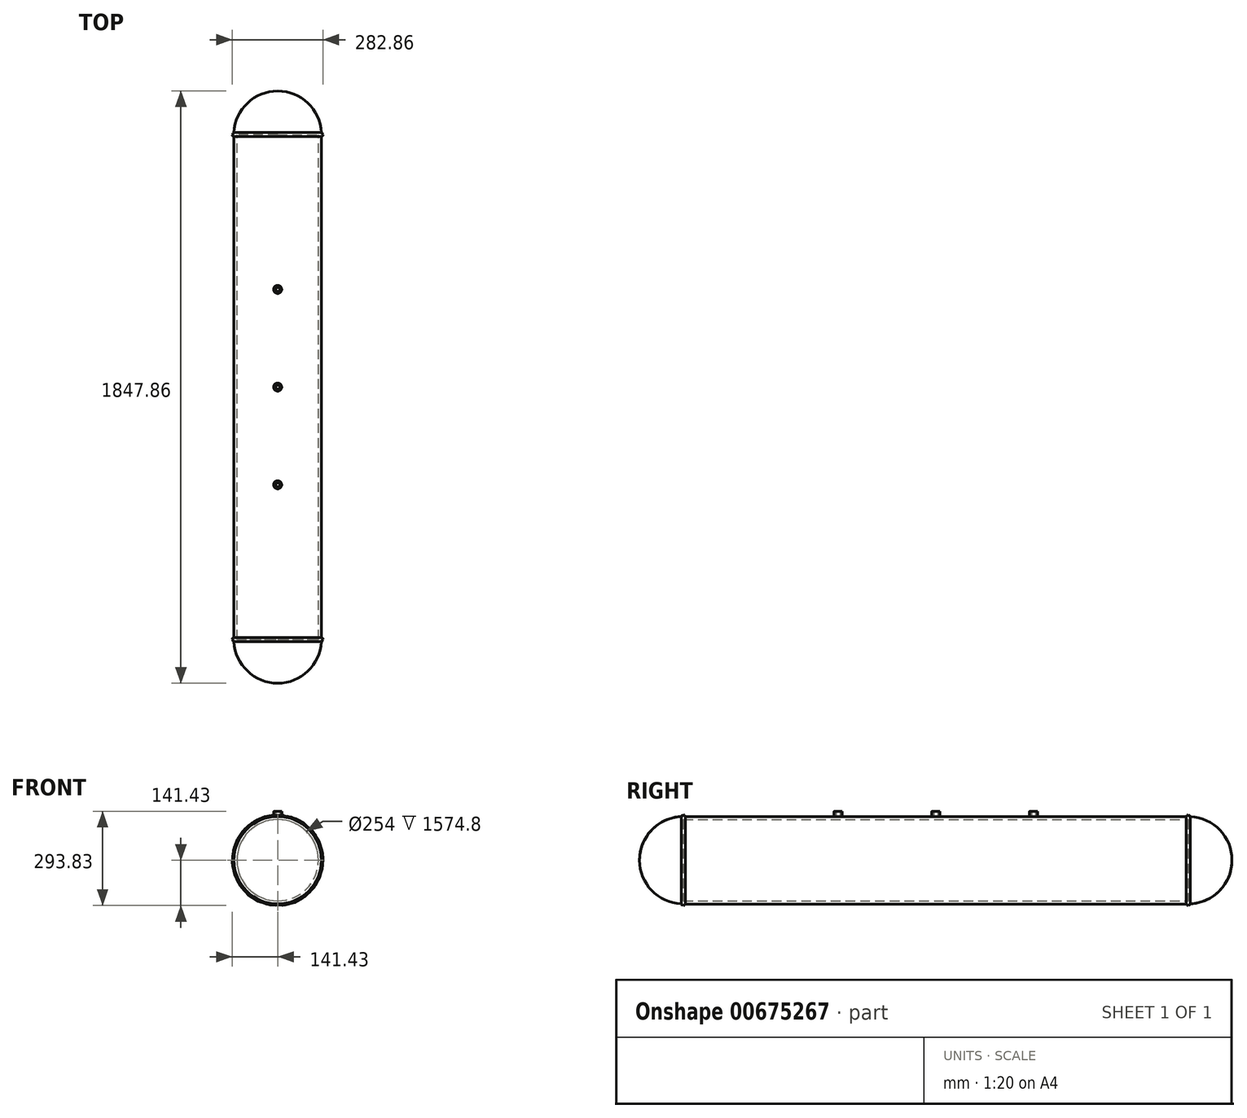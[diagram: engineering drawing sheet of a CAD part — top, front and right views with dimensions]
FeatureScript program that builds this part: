
annotation { "Feature Type Name" : "Feature", "Feature Type Description" : "" }
export const myFeature = defineFeature(function(context is Context, id is Id, definition is map)
    precondition{}
    {
        {
            var Q0;
            Q0=qCreatedBy(makeId("Front.planeOp"),FACE);
            var sketch = newSketch(context, id + "F0", { "sketchPlane" : qUnion([Q0])});
            skCircle(sketch, "E0", {"center": v(0, 0) * mm, "radius": 127 * mm});
            skCircle(sketch, "E1", {"center": v(0, 0) * mm, "radius": 136.53 * mm});
            skSolve(sketch);
        }
        {
            var Q0;
            Q0 = qSketchRegion(id + "F0", true);
            extrude(context, id + "F1", {"entities" : qUnion([Q0]), "depth" : 1574.8 * mm, "offsetDistance" : 25.4 * mm});
        }
        {
            var Q0;
            Q0=qCreatedBy(makeId("Right.planeOp"),FACE);
            var sketch = newSketch(context, id + "F2", { "sketchPlane" : qUnion([Q0])});
            skArc(sketch, "E2", {"start": v(136.53, 0) * mm, "mid": v(96.54, 96.54) * mm, "end": v(0, 136.53) * mm});
            skLineSegment(sketch, "E3", {"start": v(0, 0) * mm, "end": v(136.53, 0) * mm});
            skLineSegment(sketch, "E4", {"start": v(0, 0) * mm, "end": v(0, 136.53) * mm});
            skFitSpline(sketch, "E5", {"points": [v(6.85, 136.35) * mm, v(3.77, 140.38) * mm, v(2.34, 139.4) * mm, v(1.36, 138.73) * mm, v(-1.39, 141.15) * mm, v(-3.58, 140.82) * mm, v(-4.57, 137.53) * mm, v(-6, 136.54) * mm], "startDerivative": vector(-15.92, 29.94) * mm, "endDerivative": vector(-14.27, -5.02) * mm});
            skLineSegment(sketch, "E6", {"start": v(6.85, 136.35) * mm, "end": v(-6, 136.54) * mm});
            skLineSegment(sketch, "E7", {"start": v(0, 0) * mm, "end": v(-787.4, 0) * mm});
            skLineSegment(sketch, "E8", {"start": v(-787.4, 197.19) * mm, "end": v(-787.4, -257.38) * mm});
            skLineSegment(sketch, "E9.MirrorCS", {"start": v(-1581.65, 136.35) * mm, "end": v(-1568.8, 136.54) * mm});
            skFitSpline(sketch, "E10.MirrorCS", {"points": [v(-1581.65, 136.35) * mm, v(-1578.57, 140.38) * mm, v(-1577.14, 139.4) * mm, v(-1576.16, 138.73) * mm, v(-1573.41, 141.15) * mm, v(-1571.22, 140.82) * mm, v(-1570.23, 137.53) * mm, v(-1568.8, 136.54) * mm], "startDerivative": vector(15.92, 29.94) * mm, "endDerivative": vector(14.27, -5.02) * mm});
            skLineSegment(sketch, "E11.MirrorCS", {"start": v(-1574.8, 0) * mm, "end": v(-1574.8, 136.53) * mm});
            skArc(sketch, "E12.MirrorCS", {"start": v(-1711.33, 0) * mm, "mid": v(-1671.34, 96.54) * mm, "end": v(-1574.8, 136.53) * mm});
            skLineSegment(sketch, "E13.MirrorCS", {"start": v(-1574.8, 0) * mm, "end": v(-1711.33, 0) * mm});
            skLineSegment(sketch, "E14", {"start": v(-787.4, 0) * mm, "end": v(-177.8, 0) * mm});
            skLineSegment(sketch, "E15", {"start": v(-177.8, 0) * mm, "end": v(-177.8, 221.28) * mm});
            skSolve(sketch);
        }
        {
            var Q0;
            Q0 = qSketchRegion(id + "F2", true);
            var Q1;
            Q1=sQuery(id+"F2.wireOp",EDGE,"E7");
            revolve(context, id + "F3", {"operationType" : NewBodyOperationType.ADD, "entities" : qUnion([Q0]), "axis" : qUnion([Q1]), "revolveType" : RevolveType.FULL});
        }
        {
            var Q0;
            Q0=qCreatedBy(makeId("Top.planeOp"),FACE);
            cPlane(context, id + "F4", {"entities" : qUnion([Q0]), "cplaneType" : CPlaneType.OFFSET, "offset" : 127 * mm, "width" : 152.4 * mm, "height" : 152.4 * mm});
        }
        {
            var Q0;
            Q0=qCreatedBy(id+"F4.planeOp",FACE);
            var sketch = newSketch(context, id + "F5", { "sketchPlane" : qUnion([Q0])});
            skCircle(sketch, "E16", {"center": v(0, -787.4) * mm, "radius": 12.7 * mm});
            skCircle(sketch, "E17", {"center": v(0, -787.4) * mm, "radius": 6.35 * mm});
            skCircle(sketch, "E18", {"center": v(0, -482.6) * mm, "radius": 6.35 * mm});
            skCircle(sketch, "E19", {"center": v(0, -482.6) * mm, "radius": 12.7 * mm});
            skCircle(sketch, "E20", {"center": v(0, -1092.2) * mm, "radius": 6.35 * mm});
            skCircle(sketch, "E21", {"center": v(0, -1092.2) * mm, "radius": 12.7 * mm});
            skSolve(sketch);
        }
        {
            var Q0;
            Q0 = qSketchRegion(id + "F5", true);
            extrude(context, id + "F6", {"entities" : qUnion([Q0]), "operationType" : NewBodyOperationType.ADD, "depth" : 25.4 * mm, "offsetDistance" : 25.4 * mm});
        }
    });
